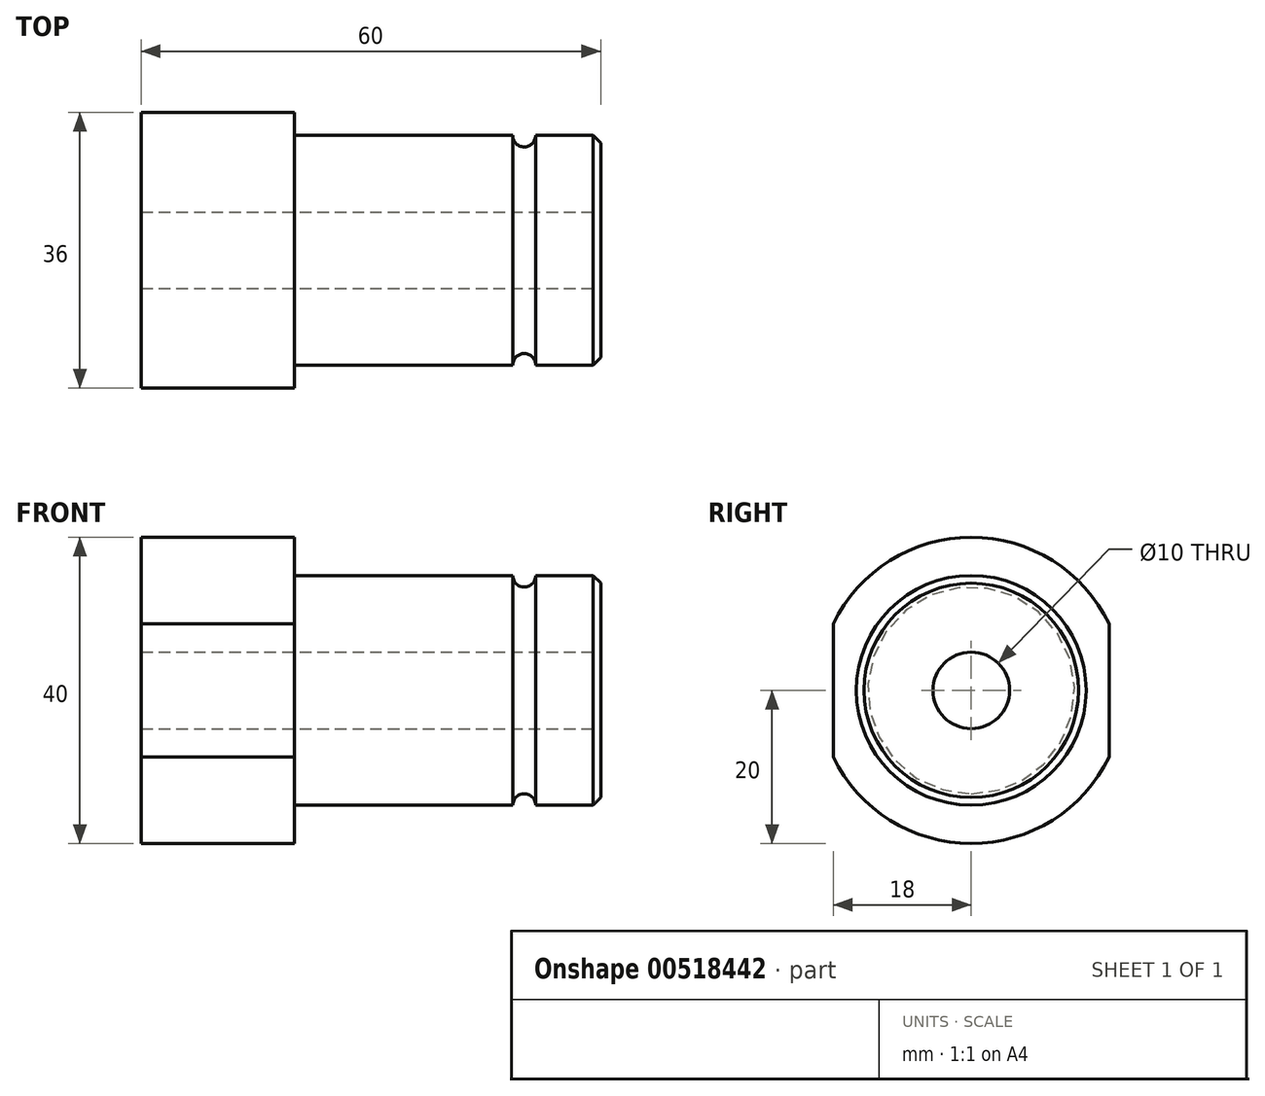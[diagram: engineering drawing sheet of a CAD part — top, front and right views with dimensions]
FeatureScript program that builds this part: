
annotation { "Feature Type Name" : "Feature", "Feature Type Description" : "" }
export const myFeature = defineFeature(function(context is Context, id is Id, definition is map)
    precondition{}
    {
        {
            assignVariable(context, id + "F0", {"name" : "A", "anyValue" : 40});
        }
        {
            var Q0;
            Q0=qCreatedBy(makeId("Right.planeOp"),FACE);
            var sketch = newSketch(context, id + "F1", { "sketchPlane" : qUnion([Q0])});
            skCircle(sketch, "E0", {"center": v(0, 0) * mm, "radius": 20 * mm});
            skSolve(sketch);
        }
        {
            var Q0;
            Q0=makeQuery(id+"F1.imprint","IMPRINT",FACE,{"disambiguationData":[TD([[makeQuery(id+"F1.imprint","IMPRINT",EDGE,{"derivedFrom":sQuery(id+"F1.wireOp",EDGE,"E0")}),1.0]])]});
            extrude(context, id + "F2", {"entities" : qUnion([Q0]), "depth" : 20 * mm, "offsetDistance" : 25 * mm});
        }
        {
            var Q0;
            Q0=makeQuery(id+"F2.opExtrude","CAP_FACE",FACE,{"disambiguationData":[OSD([sQuery(id+"F1.wireOp",EDGE,"E0")])],"isStart":false});
            var sketch = newSketch(context, id + "F3", { "sketchPlane" : qUnion([Q0])});
            skCircle(sketch, "E1", {"center": v(0, 0) * mm, "radius": 5 * mm});
            skSolve(sketch);
        }
        {
            var Q0;
            Q0=makeQuery(id+"F3.imprint","IMPRINT",FACE,{"disambiguationData":[TD([[makeQuery(id+"F3.imprint","IMPRINT",EDGE,{"derivedFrom":sQuery(id+"F3.wireOp",EDGE,"E1")}),1.0]])]});
            extrude(context, id + "F4", {"entities" : qUnion([Q0]), "operationType" : NewBodyOperationType.REMOVE, "endBound" : BoundingType.UP_TO_NEXT, "oppositeDirection" : true, "depth" : 25 * mm, "offsetDistance" : 25 * mm});
        }
        {
            var Q0;
            Q0=makeQuery(id+"F2.opExtrude","CAP_FACE",FACE,{"disambiguationData":[OSD([sQuery(id+"F1.wireOp",EDGE,"E0")])],"isStart":false});
            var sketch = newSketch(context, id + "F5", { "sketchPlane" : qUnion([Q0])});
            skLineSegment(sketch, "E2", {"start": v(-18, 0) * mm, "end": v(18, 0) * mm});
            skLineSegment(sketch, "E3", {"start": v(-18, 0) * mm, "end": v(-18, 8.72) * mm});
            skLineSegment(sketch, "E4", {"start": v(-18, 0) * mm, "end": v(-18, -8.72) * mm});
            skLineSegment(sketch, "E5", {"start": v(18, 0) * mm, "end": v(18, 8.72) * mm});
            skLineSegment(sketch, "E6", {"start": v(18, 0) * mm, "end": v(18, -8.72) * mm});
            skSolve(sketch);
        }
        {
            var Q0;
            {var subQ0=sQuery(id+"F5.wireOp",EDGE,"E3");Q0=makeQuery(id+"F5.imprint","IMPRINT",FACE,{"disambiguationData":[TD([[makeQuery(id+"F5.imprint","IMPRINT",EDGE,{"derivedFrom":subQ0}),1.0]])]});}
            var Q1;
            {var subQ0=sQuery(id+"F5.wireOp",EDGE,"E5");Q1=makeQuery(id+"F5.imprint","IMPRINT",FACE,{"disambiguationData":[TD([[makeQuery(id+"F5.imprint","IMPRINT",EDGE,{"derivedFrom":subQ0}),-1.0]])]});}
            extrude(context, id + "F6", {"entities" : qUnion([Q0, Q1]), "operationType" : NewBodyOperationType.REMOVE, "endBound" : BoundingType.UP_TO_NEXT, "oppositeDirection" : true, "depth" : 25 * mm, "offsetDistance" : 25 * mm});
        }
        {
            var Q0;
            Q0=makeQuery(id+"F2.opExtrude","CAP_FACE",FACE,{"disambiguationData":[OSD([sQuery(id+"F1.wireOp",EDGE,"E0")])],"isStart":false});
            var sketch = newSketch(context, id + "F7", { "sketchPlane" : qUnion([Q0])});
            skCircle(sketch, "E7", {"center": v(0, 0) * mm, "radius": 15 * mm});
            skSolve(sketch);
        }
        {
            var Q0;
            Q0=makeQuery(id+"F7.imprint","IMPRINT",FACE,{"disambiguationData":[TD([[makeQuery(id+"F7.imprint","IMPRINT",EDGE,{"derivedFrom":sQuery(id+"F7.wireOp",EDGE,"E7")}),1.0]])]});
            extrude(context, id + "F8", {"entities" : qUnion([Q0]), "operationType" : NewBodyOperationType.ADD, "depth" : (getVariable(context, 'A')) * mm, "offsetDistance" : 25 * mm});
        }
        {
            var Q0;
            Q0=makeQuery(id+"F8.opExtrude","CAP_EDGE",EDGE,{"disambiguationData":[OSD([sQuery(id+"F7.wireOp",EDGE,"E7")])],"isStart":false});
            chamfer(context, id + "F9", {"entities" : qUnion([Q0]), "width" : 1 * mm, "tangentPropagation" : true});
        }
        {
            var Q0;
            Q0=qCreatedBy(makeId("Front.planeOp"),FACE);
            var sketch = newSketch(context, id + "F10", { "sketchPlane" : qUnion([Q0])});
            skLineSegment(sketch, "E8", {"start": v(50, 15) * mm, "end": v(50, -15) * mm});
            skCircle(sketch, "E9", {"center": v(50, 15) * mm, "radius": 1.5 * mm});
            skSolve(sketch);
        }
        {
            var Q0;
            Q0=makeQuery(id+"F10.imprint","IMPRINT",FACE,{"disambiguationData":[TD([[makeQuery(id+"F10.imprint","IMPRINT",EDGE,{"derivedFrom":sQuery(id+"F10.wireOp",EDGE,"E9")}),1.0]])]});
            var Q1;
            Q1=makeQuery(id+"F8.opExtrude","SWEPT_FACE",FACE,{"disambiguationData":[OSD([sQuery(id+"F7.wireOp",EDGE,"E7")])]});
            revolve(context, id + "F11", {"operationType" : NewBodyOperationType.REMOVE, "entities" : qUnion([Q0]), "axis" : qUnion([Q1]), "revolveType" : RevolveType.FULL});
        }
    });
